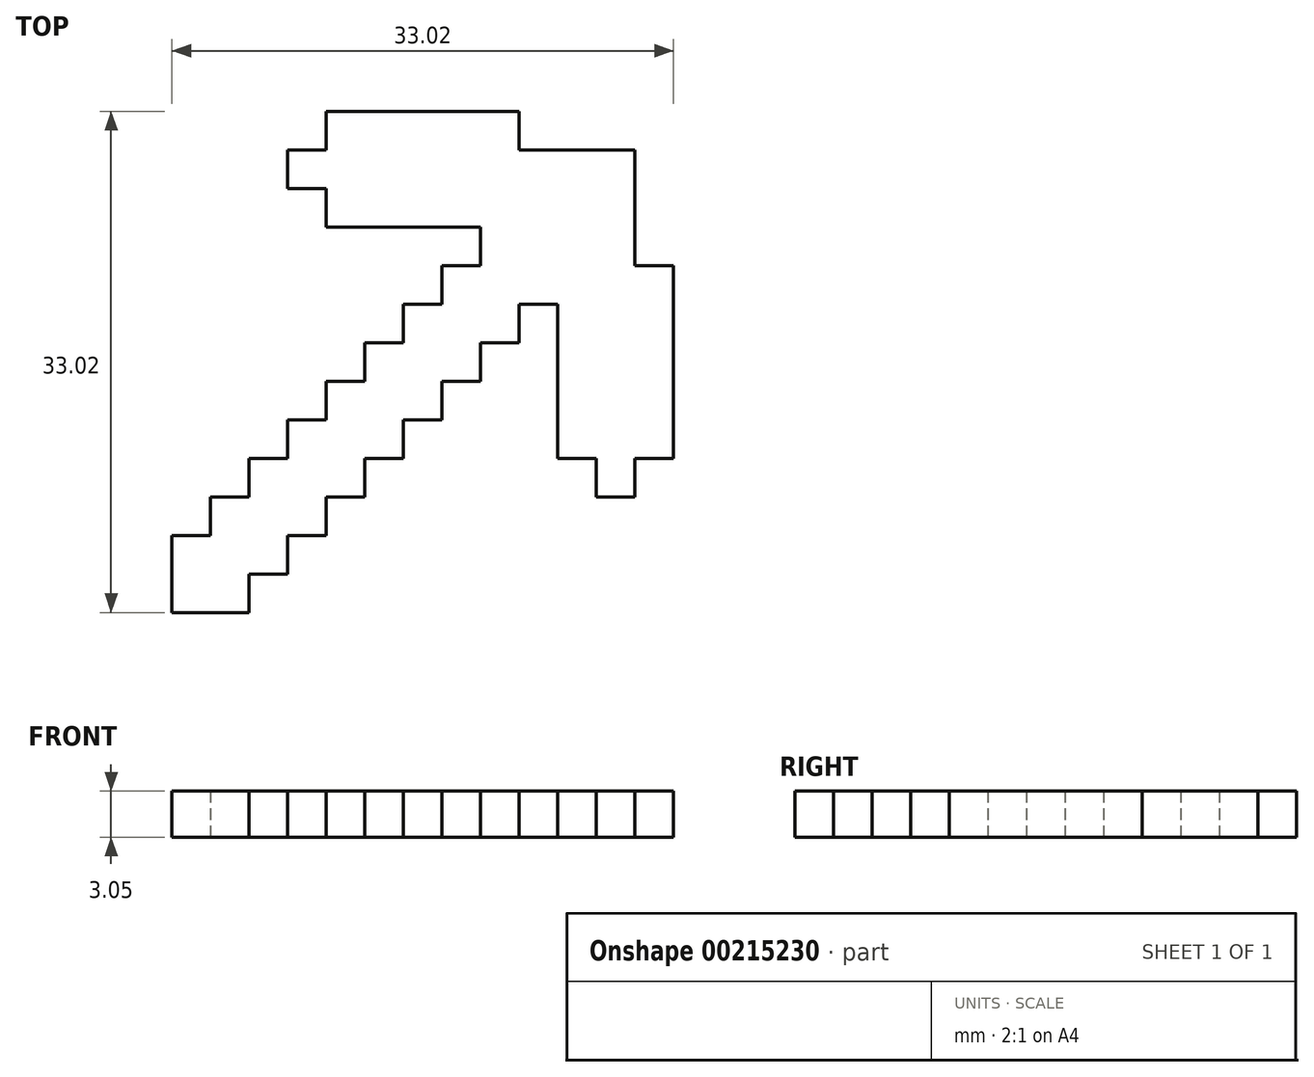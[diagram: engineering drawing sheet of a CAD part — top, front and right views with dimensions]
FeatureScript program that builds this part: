
annotation { "Feature Type Name" : "Feature", "Feature Type Description" : "" }
export const myFeature = defineFeature(function(context is Context, id is Id, definition is map)
    precondition{}
    {
        {
            var Q0;
            Q0=qCreatedBy(makeId("Top.planeOp"),FACE);
            var sketch = newSketch(context, id + "F0", { "sketchPlane" : qUnion([Q0])});
            skLineSegment(sketch, "E0", {"start": v(-30.48, -32.65) * mm, "end": v(-25.4, -32.65) * mm});
            skLineSegment(sketch, "E1", {"start": v(-25.4, -32.65) * mm, "end": v(-25.4, -30.1) * mm});
            skLineSegment(sketch, "E2", {"start": v(-25.4, -30.1) * mm, "end": v(-22.86, -30.1) * mm});
            skLineSegment(sketch, "E3", {"start": v(-22.86, -30.1) * mm, "end": v(-22.86, -27.57) * mm});
            skLineSegment(sketch, "E4", {"start": v(-22.86, -27.57) * mm, "end": v(-20.32, -27.57) * mm});
            skLineSegment(sketch, "E5", {"start": v(-20.32, -27.57) * mm, "end": v(-20.32, -25.03) * mm});
            skLineSegment(sketch, "E6", {"start": v(-20.32, -25.03) * mm, "end": v(-17.78, -25.03) * mm});
            skLineSegment(sketch, "E7", {"start": v(-17.78, -25.03) * mm, "end": v(-17.78, -22.49) * mm});
            skLineSegment(sketch, "E8", {"start": v(-17.78, -22.49) * mm, "end": v(-15.24, -22.49) * mm});
            skLineSegment(sketch, "E9", {"start": v(-15.24, -22.49) * mm, "end": v(-15.24, -19.95) * mm});
            skLineSegment(sketch, "E10", {"start": v(-15.24, -19.95) * mm, "end": v(-12.7, -19.95) * mm});
            skLineSegment(sketch, "E11", {"start": v(-12.7, -19.95) * mm, "end": v(-12.7, -17.4) * mm});
            skLineSegment(sketch, "E12", {"start": v(-12.7, -17.4) * mm, "end": v(-10.16, -17.4) * mm});
            skLineSegment(sketch, "E13", {"start": v(-10.16, -17.4) * mm, "end": v(-10.16, -14.87) * mm});
            skLineSegment(sketch, "E14", {"start": v(-10.16, -14.87) * mm, "end": v(-7.62, -14.87) * mm});
            skLineSegment(sketch, "E15", {"start": v(-7.62, -14.87) * mm, "end": v(-7.62, -12.33) * mm});
            skLineSegment(sketch, "E16", {"start": v(-30.48, -32.65) * mm, "end": v(-30.48, -27.57) * mm});
            skLineSegment(sketch, "E17", {"start": v(-30.48, -27.57) * mm, "end": v(-27.94, -27.57) * mm});
            skLineSegment(sketch, "E18", {"start": v(-27.94, -27.57) * mm, "end": v(-27.94, -25.03) * mm});
            skLineSegment(sketch, "E19", {"start": v(-27.94, -25.03) * mm, "end": v(-25.4, -25.03) * mm});
            skLineSegment(sketch, "E20", {"start": v(-25.4, -25.03) * mm, "end": v(-25.4, -22.49) * mm});
            skLineSegment(sketch, "E21", {"start": v(-25.4, -22.49) * mm, "end": v(-22.86, -22.49) * mm});
            skLineSegment(sketch, "E22", {"start": v(-22.86, -22.49) * mm, "end": v(-22.86, -19.95) * mm});
            skLineSegment(sketch, "E23", {"start": v(-22.86, -19.95) * mm, "end": v(-20.32, -19.95) * mm});
            skLineSegment(sketch, "E24", {"start": v(-20.32, -19.95) * mm, "end": v(-20.32, -17.4) * mm});
            skLineSegment(sketch, "E25", {"start": v(-20.32, -17.4) * mm, "end": v(-17.78, -17.4) * mm});
            skLineSegment(sketch, "E26", {"start": v(-17.78, -17.4) * mm, "end": v(-17.78, -14.87) * mm});
            skLineSegment(sketch, "E27", {"start": v(-17.78, -14.87) * mm, "end": v(-15.24, -14.87) * mm});
            skLineSegment(sketch, "E28", {"start": v(-15.24, -14.87) * mm, "end": v(-15.24, -12.33) * mm});
            skLineSegment(sketch, "E29", {"start": v(-15.24, -12.33) * mm, "end": v(-12.7, -12.33) * mm});
            skLineSegment(sketch, "E30", {"start": v(-12.7, -12.33) * mm, "end": v(-12.7, -9.79) * mm});
            skLineSegment(sketch, "E31", {"start": v(-5.08, -22.49) * mm, "end": v(-2.54, -22.49) * mm});
            skLineSegment(sketch, "E32", {"start": v(-2.54, -22.49) * mm, "end": v(-2.54, -25.03) * mm});
            skLineSegment(sketch, "E33", {"start": v(-2.54, -25.03) * mm, "end": v(0, -25.03) * mm});
            skLineSegment(sketch, "E34", {"start": v(0, -25.03) * mm, "end": v(0, -22.49) * mm});
            skLineSegment(sketch, "E35", {"start": v(0, -22.49) * mm, "end": v(2.54, -22.49) * mm});
            skLineSegment(sketch, "E36", {"start": v(-12.7, -9.79) * mm, "end": v(-10.16, -9.79) * mm});
            skLineSegment(sketch, "E37", {"start": v(-7.62, -12.33) * mm, "end": v(-5.08, -12.33) * mm});
            skLineSegment(sketch, "E38", {"start": v(-5.08, -12.33) * mm, "end": v(-5.08, -22.49) * mm});
            skLineSegment(sketch, "E39", {"start": v(2.54, -22.49) * mm, "end": v(2.54, -9.79) * mm});
            skLineSegment(sketch, "E40", {"start": v(-10.16, -9.79) * mm, "end": v(-10.16, -7.25) * mm});
            skLineSegment(sketch, "E41", {"start": v(-10.16, -7.25) * mm, "end": v(-20.32, -7.25) * mm});
            skLineSegment(sketch, "E42", {"start": v(-20.32, -7.25) * mm, "end": v(-20.32, -4.7) * mm});
            skLineSegment(sketch, "E43", {"start": v(-22.86, -4.7) * mm, "end": v(-20.32, -4.7) * mm});
            skLineSegment(sketch, "E44", {"start": v(-22.86, -4.7) * mm, "end": v(-22.86, -2.17) * mm});
            skLineSegment(sketch, "E45", {"start": v(-20.32, -2.17) * mm, "end": v(-22.86, -2.17) * mm});
            skLineSegment(sketch, "E46", {"start": v(-20.32, -2.17) * mm, "end": v(-20.32, 0.37) * mm});
            skLineSegment(sketch, "E47", {"start": v(-20.32, 0.37) * mm, "end": v(-7.62, 0.37) * mm});
            skLineSegment(sketch, "E48", {"start": v(-7.62, 0.37) * mm, "end": v(-7.62, -2.17) * mm});
            skLineSegment(sketch, "E49", {"start": v(2.54, -9.79) * mm, "end": v(0, -9.79) * mm});
            skLineSegment(sketch, "E50", {"start": v(0, -9.79) * mm, "end": v(0, -2.17) * mm});
            skLineSegment(sketch, "E51", {"start": v(-7.62, -2.17) * mm, "end": v(0, -2.17) * mm});
            skSolve(sketch);
        }
        {
            var Q0;
            Q0=makeQuery(id+"F0.imprint","IMPRINT",FACE,{"disambiguationData":[TD([[makeQuery(id+"F0.imprint","IMPRINT",EDGE,{"derivedFrom":sQuery(id+"F0.wireOp",EDGE,"E0")}),1.0]])]});
            extrude(context, id + "F1", {"entities" : qUnion([Q0]), "depth" : 3.05 * mm});
        }
    });
